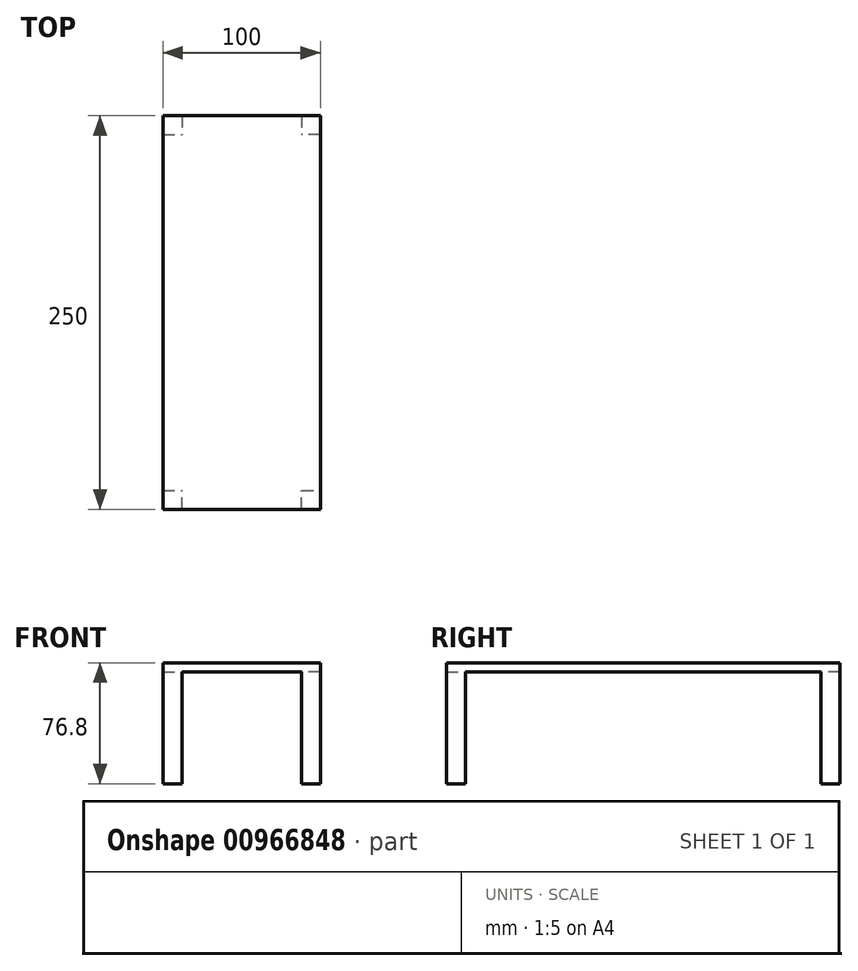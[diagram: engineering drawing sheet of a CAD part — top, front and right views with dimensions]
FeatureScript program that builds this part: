
annotation { "Feature Type Name" : "Feature", "Feature Type Description" : "" }
export const myFeature = defineFeature(function(context is Context, id is Id, definition is map)
    precondition{}
    {
        {
            var Q0;
            Q0=qCreatedBy(makeId("Top.planeOp"),FACE);
            var sketch = newSketch(context, id + "F0", { "sketchPlane" : qUnion([Q0])});
            skLineSegment(sketch, "E0.bottom", {"start": v(-50, 125) * mm, "end": v(50, 125) * mm});
            skLineSegment(sketch, "E0.top", {"start": v(-50, -125) * mm, "end": v(50, -125) * mm});
            skLineSegment(sketch, "E0.left", {"start": v(-50, 125) * mm, "end": v(-50, -125) * mm});
            skLineSegment(sketch, "E0.right", {"start": v(50, 125) * mm, "end": v(50, -125) * mm});
            skLineSegment(sketch, "E1", {"start": v(-50, 125) * mm, "end": v(50, -125) * mm, "construction": true});
            skSolve(sketch);
        }
        {
            var Q0;
            Q0=makeQuery(id+"F0.imprint","IMPRINT",FACE,{"disambiguationData":[TD([[makeQuery(id+"F0.imprint","IMPRINT",EDGE,{"derivedFrom":sQuery(id+"F0.wireOp",EDGE,"E0.bottom")}),-1.0]])]});
            extrude(context, id + "F1", {"entities" : qUnion([Q0]), "depth" : 5.8 * mm, "offsetDistance" : 25 * mm});
        }
        {
            var Q0;
            Q0=makeQuery(id+"F1.opExtrude","CAP_FACE",FACE,{"disambiguationData":[OSD([sQuery(id+"F0.wireOp",EDGE,"E0.bottom"),sQuery(id+"F0.wireOp",EDGE,"E0.top"),sQuery(id+"F0.wireOp",EDGE,"E0.left"),sQuery(id+"F0.wireOp",EDGE,"E0.right")])],"isStart":true});
            var sketch = newSketch(context, id + "F2", { "sketchPlane" : qUnion([Q0])});
            skLineSegment(sketch, "E2.bottom", {"start": v(-50, 125) * mm, "end": v(-38, 125) * mm});
            skLineSegment(sketch, "E2.top", {"start": v(-50, 113) * mm, "end": v(-38, 113) * mm});
            skLineSegment(sketch, "E2.left", {"start": v(-50, 125) * mm, "end": v(-50, 113) * mm});
            skLineSegment(sketch, "E2.right", {"start": v(-38, 125) * mm, "end": v(-38, 113) * mm});
            skLineSegment(sketch, "E3.bottom", {"start": v(38, 125) * mm, "end": v(50, 125) * mm});
            skLineSegment(sketch, "E3.top", {"start": v(38, 113) * mm, "end": v(50, 113) * mm});
            skLineSegment(sketch, "E3.left", {"start": v(38, 125) * mm, "end": v(38, 113) * mm});
            skLineSegment(sketch, "E3.right", {"start": v(50, 125) * mm, "end": v(50, 113) * mm});
            skLineSegment(sketch, "E4.bottom", {"start": v(50, -125) * mm, "end": v(38, -125) * mm});
            skLineSegment(sketch, "E4.top", {"start": v(50, -113) * mm, "end": v(38, -113) * mm});
            skLineSegment(sketch, "E4.left", {"start": v(50, -125) * mm, "end": v(50, -113) * mm});
            skLineSegment(sketch, "E4.right", {"start": v(38, -125) * mm, "end": v(38, -113) * mm});
            skLineSegment(sketch, "E5.bottom", {"start": v(-50, -125) * mm, "end": v(-38, -125) * mm});
            skLineSegment(sketch, "E5.top", {"start": v(-50, -113) * mm, "end": v(-38, -113) * mm});
            skLineSegment(sketch, "E5.left", {"start": v(-50, -125) * mm, "end": v(-50, -113) * mm});
            skLineSegment(sketch, "E5.right", {"start": v(-38, -125) * mm, "end": v(-38, -113) * mm});
            skSolve(sketch);
        }
        {
            var Q0;
            Q0 = qSketchRegion(id + "F2", true);
            extrude(context, id + "F3", {"entities" : qUnion([Q0]), "operationType" : NewBodyOperationType.ADD, "depth" : 71 * mm, "offsetDistance" : 25 * mm});
        }
    });
